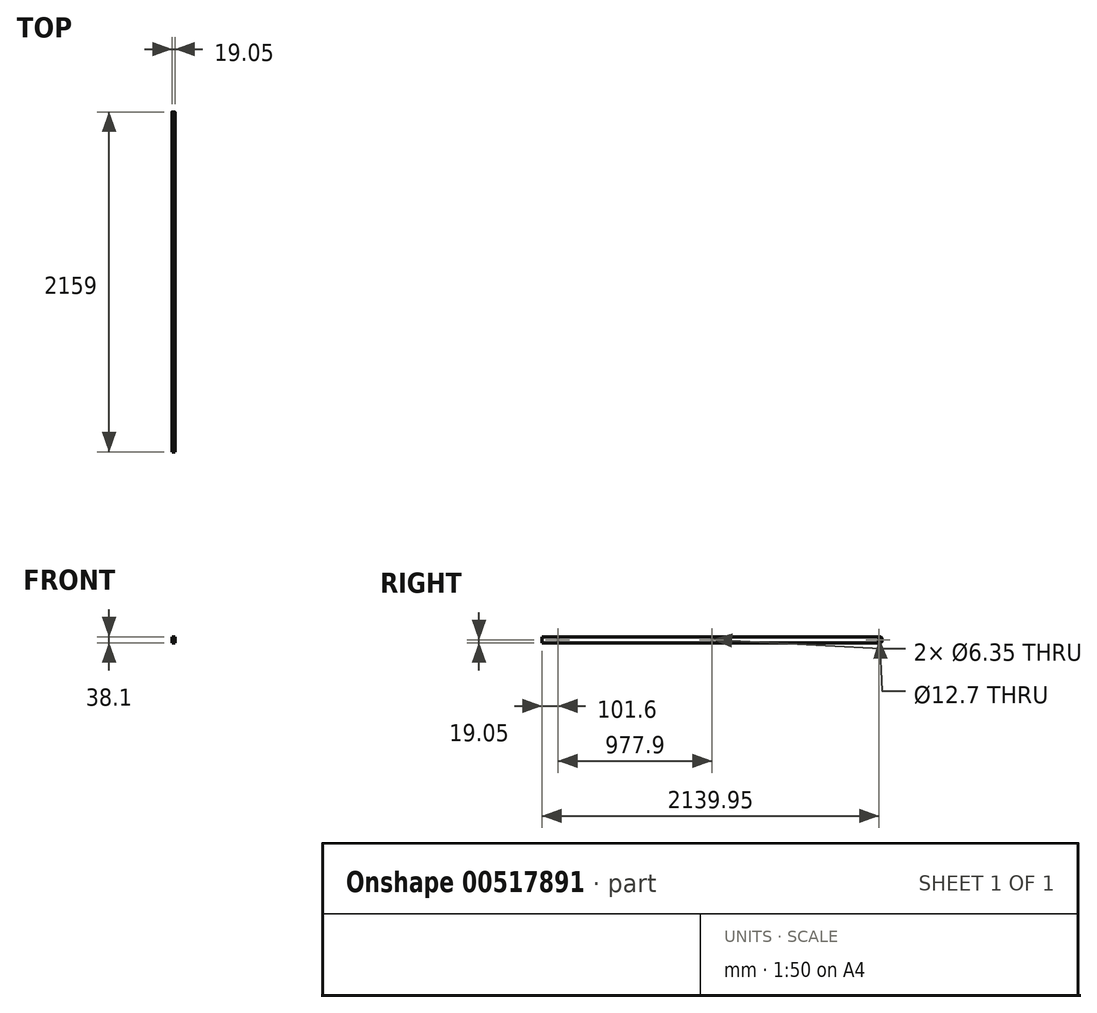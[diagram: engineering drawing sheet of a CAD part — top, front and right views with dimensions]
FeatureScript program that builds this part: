
annotation { "Feature Type Name" : "Feature", "Feature Type Description" : "" }
export const myFeature = defineFeature(function(context is Context, id is Id, definition is map)
    precondition{}
    {
        {
            var Q0;
            Q0=qCreatedBy(makeId("Front.planeOp"),FACE);
            var sketch = newSketch(context, id + "F0", { "sketchPlane" : qUnion([Q0])});
            skLineSegment(sketch, "E0.bottom", {"start": v(0, 0) * mm, "end": v(19.05, 0) * mm});
            skLineSegment(sketch, "E0.top", {"start": v(0, 38.1) * mm, "end": v(19.05, 38.1) * mm});
            skLineSegment(sketch, "E0.left", {"start": v(0, 0) * mm, "end": v(0, 38.1) * mm});
            skLineSegment(sketch, "E0.right", {"start": v(19.05, 0) * mm, "end": v(19.05, 38.1) * mm});
            skLineSegment(sketch, "E1.0", {"start": v(3.17, 34.93) * mm, "end": v(15.87, 34.93) * mm, "construction": true});
            skLineSegment(sketch, "E1.1", {"start": v(3.17, 3.17) * mm, "end": v(3.17, 34.93) * mm, "construction": true});
            skLineSegment(sketch, "E1.2", {"start": v(3.17, 3.17) * mm, "end": v(15.87, 3.17) * mm, "construction": true});
            skLineSegment(sketch, "E1.3", {"start": v(15.87, 3.17) * mm, "end": v(15.87, 34.93) * mm, "construction": true});
            skSolve(sketch);
        }
        {
            var Q0;
            Q0=makeQuery(id+"F0.imprint","IMPRINT",FACE,{"disambiguationData":[TD([[makeQuery(id+"F0.imprint","IMPRINT",EDGE,{"derivedFrom":sQuery(id+"F0.wireOp",EDGE,"E0.bottom")}),1.0]])]});
            extrude(context, id + "F1", {"entities" : qUnion([Q0]), "oppositeDirection" : true, "depth" : 2159 * mm, "offsetDistance" : 25.4 * mm});
        }
        {
            var Q0;
            Q0=makeQuery(id+"F1.opExtrude","SWEPT_FACE",FACE,{"disambiguationData":[OSD([sQuery(id+"F0.wireOp",EDGE,"E0.right")])]});
            var sketch = newSketch(context, id + "F2", { "sketchPlane" : qUnion([Q0])});
            skCircle(sketch, "E2", {"center": v(2159, 19.05) * mm, "radius": 6.35 * mm, "construction": true});
            skCircle(sketch, "E3.1.0.0", {"center": v(2139.95, 19.05) * mm, "radius": 6.35 * mm});
            skLineSegment(sketch, "E3.direction1", {"start": v(2159, 19.05) * mm, "end": v(2139.95, 19.05) * mm, "construction": true});
            skCircle(sketch, "E4", {"center": v(57.15, 19.05) * mm, "radius": 3.18 * mm, "construction": true});
            skCircle(sketch, "E5.1.0.0", {"center": v(101.6, 19.05) * mm, "radius": 3.18 * mm});
            skLineSegment(sketch, "E5.direction1", {"start": v(57.15, 19.05) * mm, "end": v(101.6, 19.05) * mm, "construction": true});
            skCircle(sketch, "E6", {"center": v(1079.5, 19.05) * mm, "radius": 3.18 * mm});
            skPoint(sketch, "E6.centerSnap0", {"position": v(1079.5, 38.1) * mm});
            skSolve(sketch);
        }
        {
            var Q0;
            Q0=makeQuery(id+"F2.imprint","IMPRINT",FACE,{"disambiguationData":[TD([[makeQuery(id+"F2.imprint","IMPRINT",EDGE,{"derivedFrom":sQuery(id+"F2.wireOp",EDGE,"E3.1.0.0")}),1.0]])]});
            var Q1;
            Q1=makeQuery(id+"F2.imprint","IMPRINT",FACE,{"disambiguationData":[TD([[makeQuery(id+"F2.imprint","IMPRINT",EDGE,{"derivedFrom":sQuery(id+"F2.wireOp",EDGE,"E6")}),1.0]])]});
            var Q2;
            Q2=makeQuery(id+"F2.imprint","IMPRINT",FACE,{"disambiguationData":[TD([[makeQuery(id+"F2.imprint","IMPRINT",EDGE,{"derivedFrom":sQuery(id+"F2.wireOp",EDGE,"E5.1.0.0")}),1.0]])]});
            extrude(context, id + "F3", {"entities" : qUnion([Q0, Q1, Q2]), "operationType" : NewBodyOperationType.REMOVE, "endBound" : BoundingType.THROUGH_ALL, "oppositeDirection" : true, "depth" : 25.4 * mm, "offsetDistance" : 25.4 * mm});
        }
        {
            var Q0;
            Q0=makeQuery(id+"F1.opExtrude","CAP_EDGE",EDGE,{"disambiguationData":[OSD([sQuery(id+"F0.wireOp",EDGE,"E0.top")])],"isStart":false});
            var Q1;
            Q1=makeQuery(id+"F1.opExtrude","CAP_EDGE",EDGE,{"disambiguationData":[OSD([sQuery(id+"F0.wireOp",EDGE,"E0.bottom")])],"isStart":false});
            fillet(context, id + "F4", {"entities" : qUnion([Q0, Q1]), "radius" : 12.7 * mm, "tangentPropagation" : true, "allowEdgeOverflow" : false});
        }
    });
